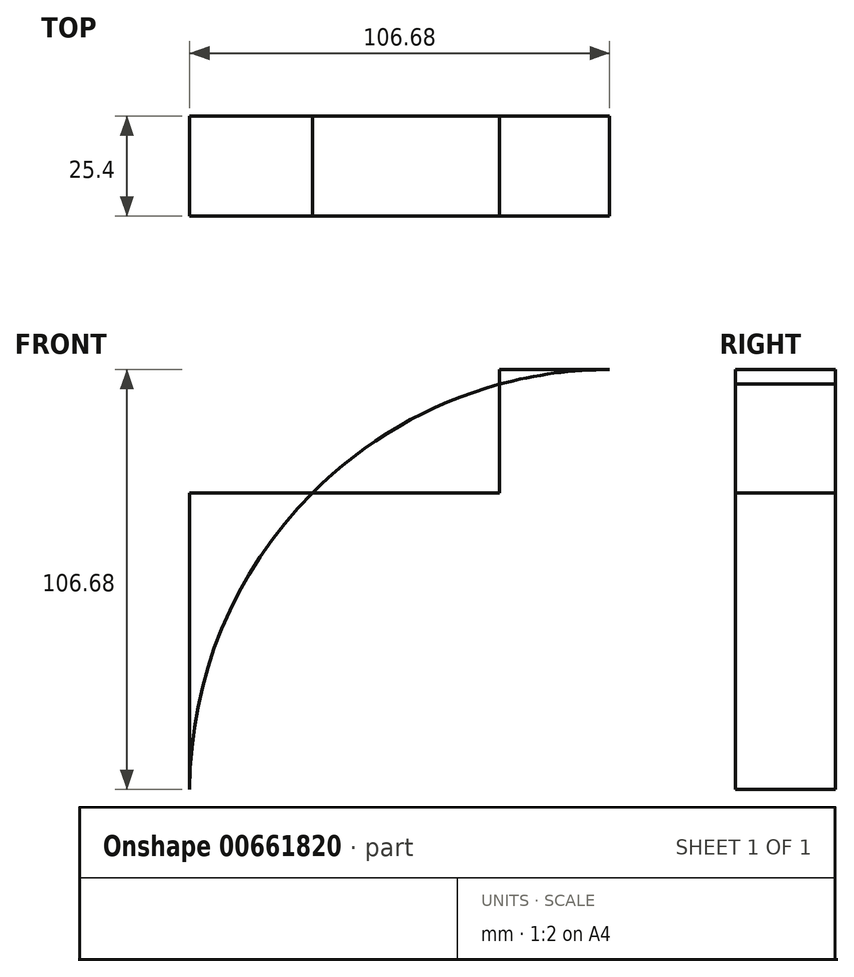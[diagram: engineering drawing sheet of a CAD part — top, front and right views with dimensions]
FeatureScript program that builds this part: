
annotation { "Feature Type Name" : "Feature", "Feature Type Description" : "" }
export const myFeature = defineFeature(function(context is Context, id is Id, definition is map)
    precondition{}
    {
        {
            var Q0;
            Q0=qCreatedBy(makeId("Front.planeOp"),FACE);
            var sketch = newSketch(context, id + "F0", { "sketchPlane" : qUnion([Q0])});
            skLineSegment(sketch, "E0.bottom", {"start": v(67.33, 15.68) * mm, "end": v(39.35, 15.68) * mm});
            skLineSegment(sketch, "E0.top", {"start": v(39.35, -15.68) * mm, "end": v(-39.35, -15.68) * mm});
            skLineSegment(sketch, "E0.left", {"start": v(39.35, 15.68) * mm, "end": v(39.35, -15.68) * mm});
            skLineSegment(sketch, "E0.right", {"start": v(-39.35, -15.68) * mm, "end": v(-39.35, -91) * mm});
            skPoint(sketch, "E0.middle", {"position": v(0, 0) * mm});
            skPoint(sketch, "E1.visualSharp", {"position": v(-39.35, 15.68) * mm});
            skArc(sketch, "E1.filletArc", {"start": v(67.33, 15.68) * mm, "mid": v(-8.1, -15.56) * mm, "end": v(-39.35, -91) * mm});
            skSolve(sketch);
        }
        {
            var Q0;
            Q0 = qSketchRegion(id + "F0", true);
            extrude(context, id + "F1", {"entities" : qUnion([Q0]), "depth" : 25.4 * mm, "offsetDistance" : 25.4 * mm});
        }
    });
